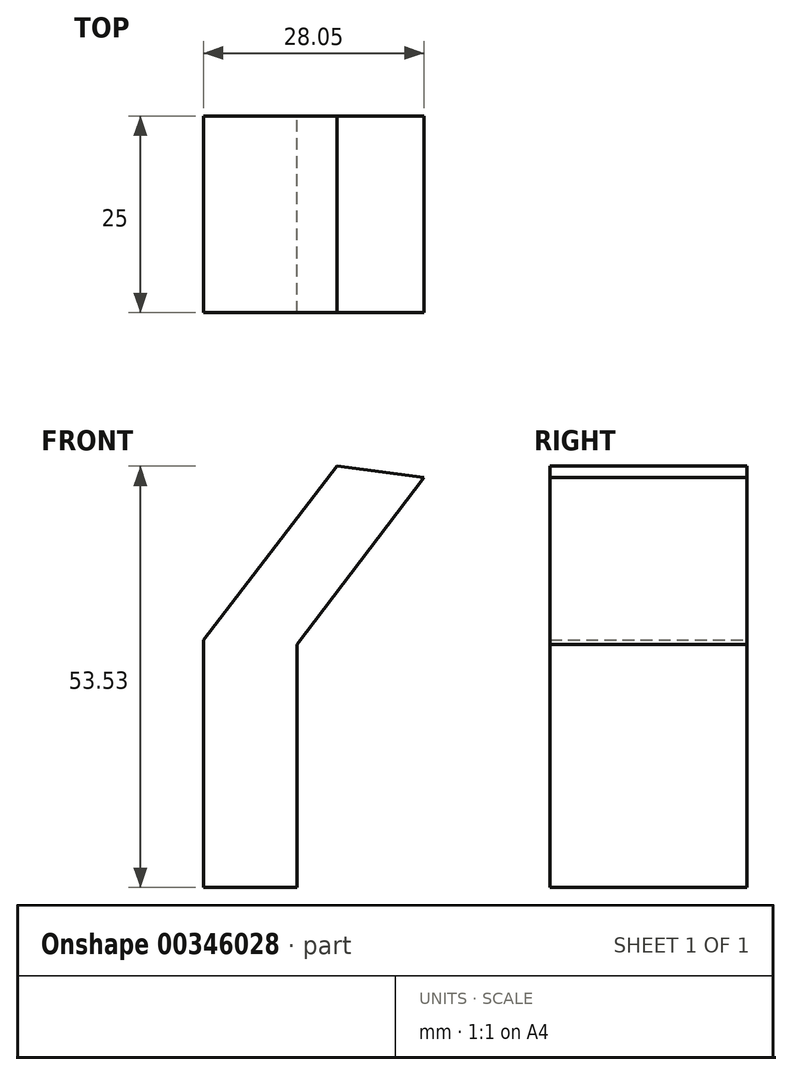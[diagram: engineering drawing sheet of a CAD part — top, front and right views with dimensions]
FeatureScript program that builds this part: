
annotation { "Feature Type Name" : "Feature", "Feature Type Description" : "" }
export const myFeature = defineFeature(function(context is Context, id is Id, definition is map)
    precondition{}
    {
        {
            var Q0;
            Q0=qCreatedBy(makeId("Front.planeOp"),FACE);
            var sketch = newSketch(context, id + "F0", { "sketchPlane" : qUnion([Q0])});
            skLineSegment(sketch, "E0", {"start": v(-20.68, 41.92) * mm, "end": v(-37.68, 19.83) * mm});
            skLineSegment(sketch, "E1", {"start": v(-37.68, 19.83) * mm, "end": v(-37.68, -11.61) * mm});
            skLineSegment(sketch, "E2", {"start": v(-37.68, -11.61) * mm, "end": v(-25.78, -11.61) * mm});
            skLineSegment(sketch, "E3", {"start": v(-25.78, -11.61) * mm, "end": v(-25.78, 19.26) * mm});
            skLineSegment(sketch, "E4", {"start": v(-25.78, 19.26) * mm, "end": v(-9.63, 40.5) * mm});
            skLineSegment(sketch, "E5", {"start": v(-9.63, 40.5) * mm, "end": v(-20.68, 41.92) * mm});
            skSolve(sketch);
        }
        {
            var Q0;
            Q0 = qSketchRegion(id + "F0", true);
            extrude(context, id + "F1", {"entities" : qUnion([Q0]), "depth" : 25 * mm});
        }
    });
